# Revit family: Haworth_Cappellini_Fronzoni64_Table_EU_PRELIMINARY
name_source: partatom
category: Furniture
revit_build: Autodesk Revit 2018 (Build: 20170223_1515(x64)
units: mm (PartAtom-declared; Revit-internal decimal feet)

## family parameters
Always vertical = Yes
Cut with Voids When Loaded = No
OmniClass Number = 23.40.70.14.64.21
OmniClass Title = Systems Furniture
Room Calculation Point = No
Shared = No
Work Plane-Based = No

## types (3) — shared parameters
Actual Depth = 100 cm
Assembly Code = E2020200
Description = Haworth - Cappellini - Fronzoni 64 - Table
Glide Offset = 1 cm
Leg Thickness = 2 cm
Manufacturer = Haworth
Model = FR_2X
Revision Number = 4
Size = Verify Final Dim. w/ Haworth
Table Top Thickness = 3 cm
URL = https://www.haworth.com
URL - Product = https://www.haworth.com
Warranty = http://www.haworth.com
zero-valued in all types: Chamfer, Glide Height

## per-type parameters (varying)
| type | Actual Height | Actual Width |
| High Rectangle | 70 cm | 200 cm |
| High Square | 70 cm | 100 cm |
| Low Square | 30 cm | 100 cm |

type visibility flags: 3 boolean params named "<type name>" — each type sets only its own to Yes (folded from table)

## geometry (parser evidence)
native form markers: Sweep x2
no freeform markers — native parametric forms only
